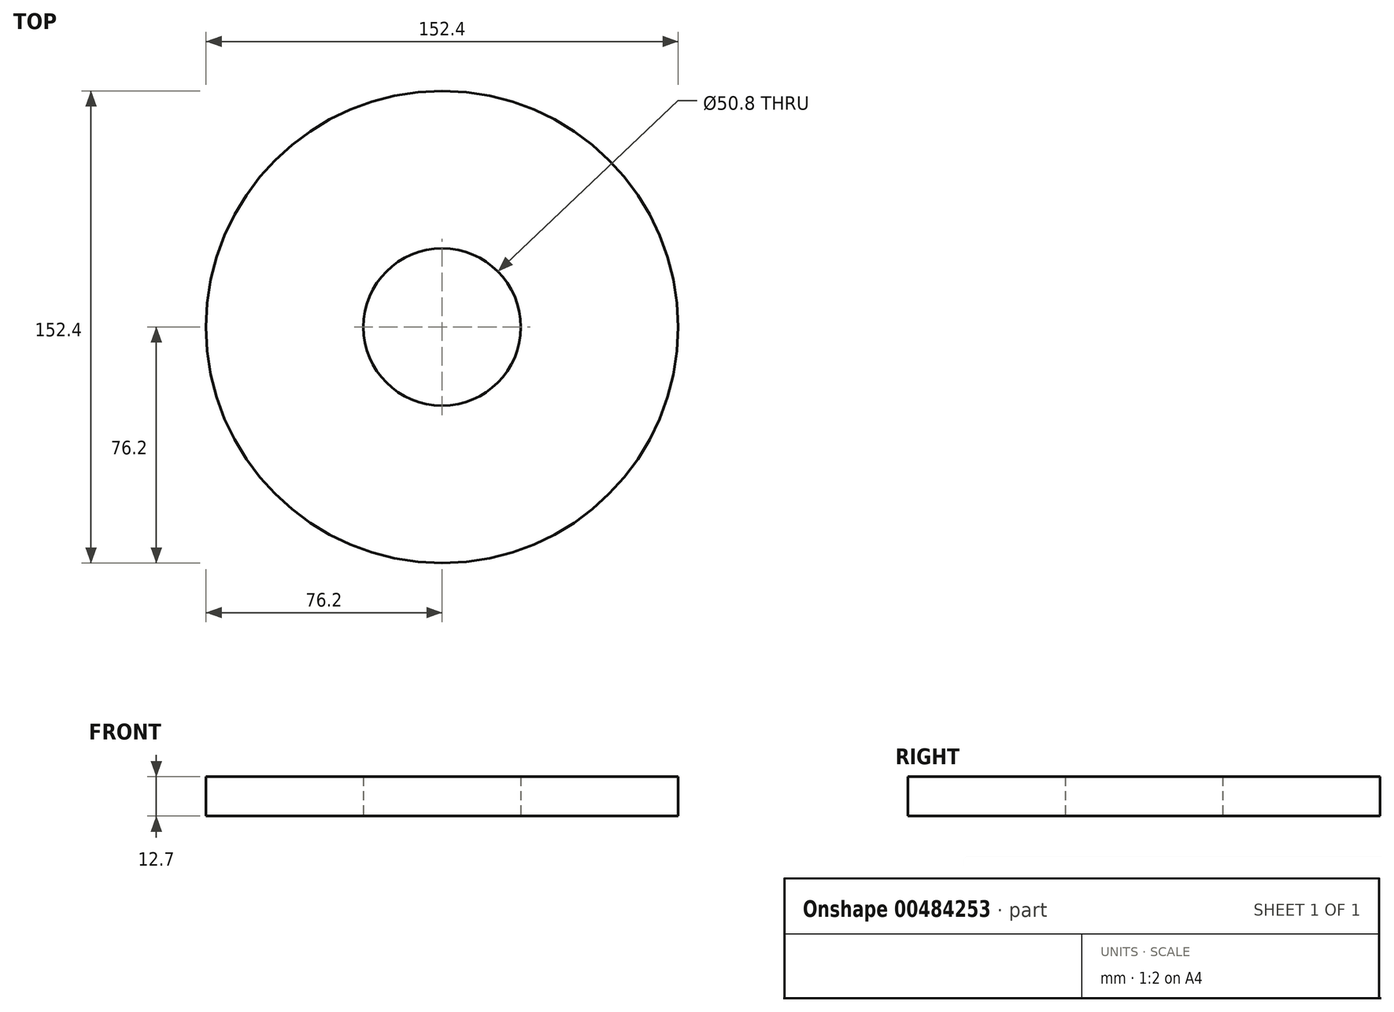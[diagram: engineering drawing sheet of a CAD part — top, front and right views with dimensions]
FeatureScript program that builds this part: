
annotation { "Feature Type Name" : "Feature", "Feature Type Description" : "" }
export const myFeature = defineFeature(function(context is Context, id is Id, definition is map)
    precondition{}
    {
        {
            var Q0;
            Q0=qCreatedBy(makeId("Top.planeOp"),FACE);
            var sketch = newSketch(context, id + "F0", { "sketchPlane" : qUnion([Q0])});
            skCircle(sketch, "E0", {"center": v(0, 0) * mm, "radius": 76.2 * mm});
            skCircle(sketch, "E1", {"center": v(0, 0) * mm, "radius": 25.4 * mm});
            skSolve(sketch);
        }
        {
            var Q0;
            Q0=makeQuery(id+"F0.imprint","IMPRINT",FACE,{"disambiguationData":[TD([[makeQuery(id+"F0.imprint","IMPRINT",EDGE,{"derivedFrom":sQuery(id+"F0.wireOp",EDGE,"E0")}),1.0]])]});
            extrude(context, id + "F1", {"entities" : qUnion([Q0]), "depth" : 12.7 * mm});
        }
    });
